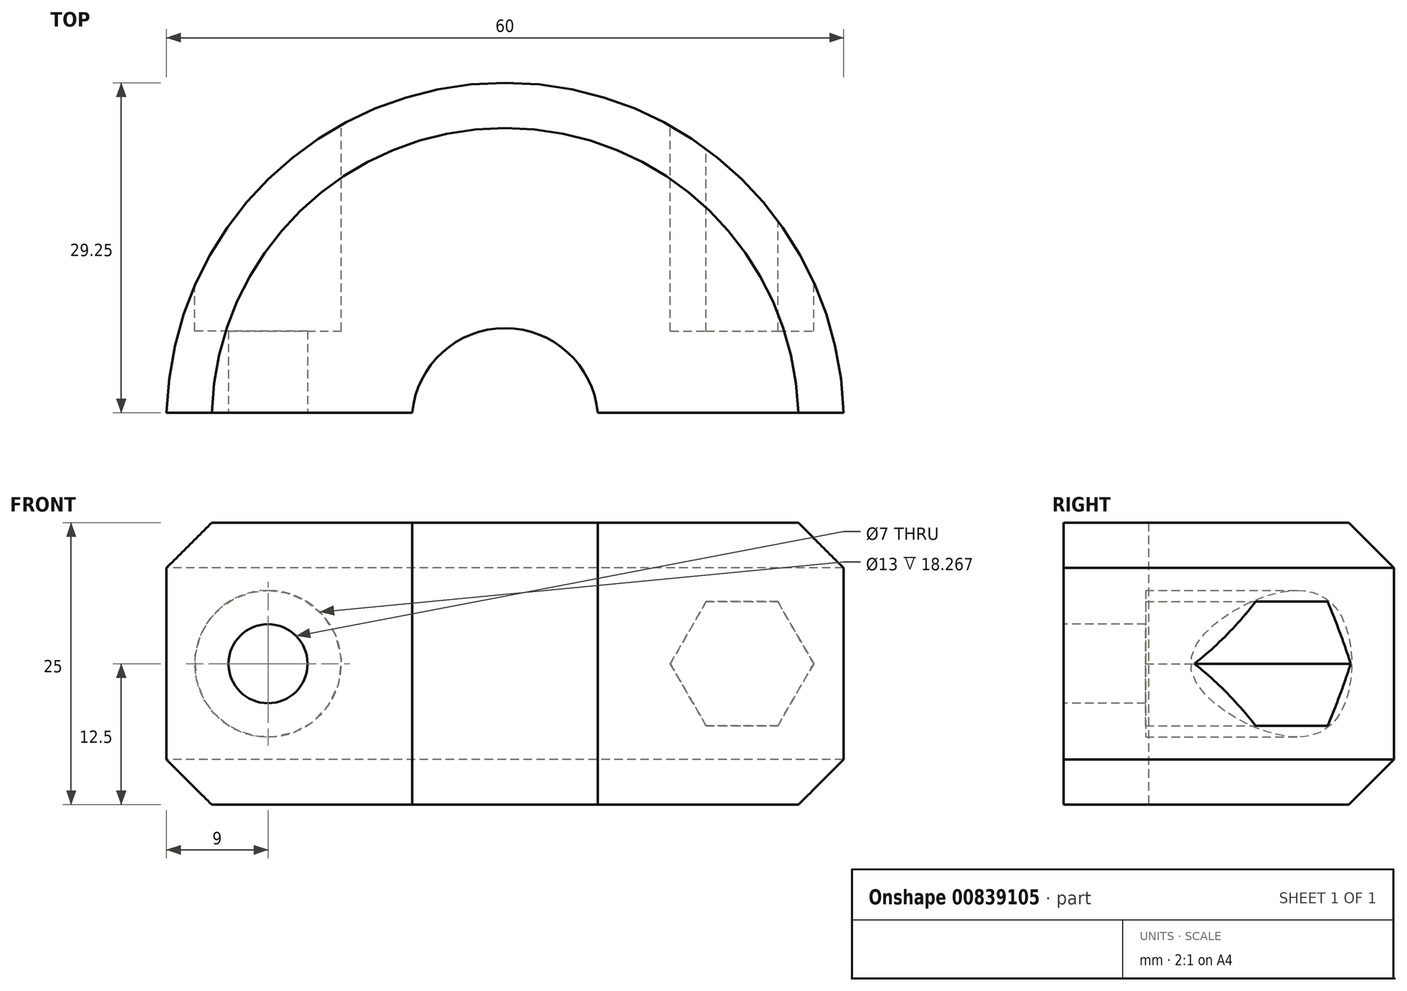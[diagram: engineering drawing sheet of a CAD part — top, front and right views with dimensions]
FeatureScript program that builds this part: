
annotation { "Feature Type Name" : "Feature", "Feature Type Description" : "" }
export const myFeature = defineFeature(function(context is Context, id is Id, definition is map)
    precondition{}
    {
        {
            var Q0;
            Q0=qCreatedBy(makeId("Top.planeOp"),FACE);
            var sketch = newSketch(context, id + "F0", { "sketchPlane" : qUnion([Q0])});
            skArc(sketch, "E0", {"start": v(30, 0) * mm, "mid": v(0, 30) * mm, "end": v(-30, 0) * mm});
            skArc(sketch, "E1", {"start": v(8.25, 0) * mm, "mid": v(0, 8.25) * mm, "end": v(-8.25, 0) * mm});
            skLineSegment(sketch, "E2", {"start": v(-41.2, 0) * mm, "end": v(58.71, 0) * mm, "construction": true});
            skLineSegment(sketch, "E3", {"start": v(-30, 0) * mm, "end": v(-8.25, 0) * mm});
            skLineSegment(sketch, "E4", {"start": v(8.25, 0) * mm, "end": v(30, 0) * mm});
            skSolve(sketch);
        }
        {
            var Q0;
            Q0=makeQuery(id+"F0.imprint","IMPRINT",FACE,{"disambiguationData":[TD([[makeQuery(id+"F0.imprint","IMPRINT",EDGE,{"derivedFrom":sQuery(id+"F0.wireOp",EDGE,"E0")}),1.0]])]});
            extrude(context, id + "F1", {"entities" : qUnion([Q0]), "depth" : 25 * mm, "offsetDistance" : 25 * mm});
        }
        {
            var Q0;
            Q0=makeQuery(id+"F1.opExtrude","SWEPT_FACE",FACE,{"disambiguationData":[OSD([sQuery(id+"F0.wireOp",EDGE,"E3")])]});
            var sketch = newSketch(context, id + "F2", { "sketchPlane" : qUnion([Q0])});
            skCircle(sketch, "E5", {"center": v(-21, 12.5) * mm, "radius": 3.5 * mm});
            skLineSegment(sketch, "E6", {"start": v(32.43, 12.5) * mm, "end": v(-38.56, 12.5) * mm, "construction": true});
            skPoint(sketch, "E6.startSnap0", {"position": v(-30, 12.5) * mm});
            skLineSegment(sketch, "E7", {"start": v(0, 0) * mm, "end": v(0, 34.25) * mm, "construction": true});
            skCircle(sketch, "E8.MirrorC", {"center": v(21, 12.5) * mm, "radius": 3.5 * mm});
            skSolve(sketch);
        }
        {
            var Q0;
            Q0=makeQuery(id+"F2.imprint","IMPRINT",FACE,{"disambiguationData":[TD([[makeQuery(id+"F2.imprint","IMPRINT",EDGE,{"derivedFrom":sQuery(id+"F2.wireOp",EDGE,"E5")}),1.0]])]});
            var Q1;
            Q1=makeQuery(id+"F2.imprint","IMPRINT",FACE,{"disambiguationData":[TD([[makeQuery(id+"F2.imprint","IMPRINT",EDGE,{"derivedFrom":sQuery(id+"F2.wireOp",EDGE,"E8.MirrorC")}),-1.0]])]});
            extrude(context, id + "F3", {"entities" : qUnion([Q0, Q1]), "operationType" : NewBodyOperationType.REMOVE, "oppositeDirection" : true, "depth" : 25 * mm, "offsetDistance" : 25 * mm});
        }
        {
            var Q0;
            Q0=qCreatedBy(makeId("Front.planeOp"),FACE);
            cPlane(context, id + "F4", {"entities" : qUnion([Q0]), "cplaneType" : CPlaneType.OFFSET, "offset" : 30 * mm, "oppositeDirection" : true, "width" : 150 * mm, "height" : 150 * mm});
        }
        {
            var Q0;
            Q0=qCreatedBy(id+"F4.planeOp",FACE);
            var sketch = newSketch(context, id + "F5", { "sketchPlane" : qUnion([Q0])});
            skCircle(sketch, "E9.cCircle", {"center": v(21, 12.5) * mm, "radius": 6.35 * mm, "construction": true});
            skLineSegment(sketch, "E9.0", {"start": v(24.18, 18) * mm, "end": v(27.35, 12.5) * mm});
            skLineSegment(sketch, "E9.1", {"start": v(27.35, 12.5) * mm, "end": v(24.18, 7) * mm});
            skLineSegment(sketch, "E9.2", {"start": v(24.18, 7) * mm, "end": v(17.82, 7) * mm});
            skLineSegment(sketch, "E9.3", {"start": v(17.82, 7) * mm, "end": v(14.65, 12.5) * mm});
            skLineSegment(sketch, "E9.4", {"start": v(14.65, 12.5) * mm, "end": v(17.82, 18) * mm});
            skLineSegment(sketch, "E9.5", {"start": v(17.82, 18) * mm, "end": v(24.18, 18) * mm});
            skCircle(sketch, "E10", {"center": v(-21, 12.5) * mm, "radius": 6.5 * mm});
            skSolve(sketch);
        }
        {
            var Q0;
            Q0=makeQuery(id+"F5.imprint","IMPRINT",FACE,{"disambiguationData":[TD([[makeQuery(id+"F5.imprint","IMPRINT",EDGE,{"derivedFrom":sQuery(id+"F5.wireOp",EDGE,"E9.0")}),-1.0]])]});
            var Q1;
            Q1=makeQuery(id+"F5.imprint","IMPRINT",FACE,{"disambiguationData":[TD([[makeQuery(id+"F5.imprint","IMPRINT",EDGE,{"derivedFrom":sQuery(id+"F5.wireOp",EDGE,"E10")}),1.0]])]});
            extrude(context, id + "F6", {"entities" : qUnion([Q0, Q1]), "operationType" : NewBodyOperationType.REMOVE, "depth" : 22 * mm, "offsetDistance" : 25 * mm});
        }
        {
            var Q0;
            Q0=makeQuery(id+"F1.opExtrude","CAP_FACE",FACE,{"disambiguationData":[OSD([sQuery(id+"F0.wireOp",EDGE,"E0"),sQuery(id+"F0.wireOp",EDGE,"E1"),sQuery(id+"F0.wireOp",EDGE,"E3"),sQuery(id+"F0.wireOp",EDGE,"E4")])],"isStart":false});
            var sketch = newSketch(context, id + "F7", { "sketchPlane" : qUnion([Q0])});
            skLineSegment(sketch, "E11.bottom", {"start": v(-30, 0) * mm, "end": v(30, 0) * mm});
            skLineSegment(sketch, "E11.top", {"start": v(-30, 0.75) * mm, "end": v(30, 0.75) * mm});
            skLineSegment(sketch, "E11.left", {"start": v(-30, 0) * mm, "end": v(-30, 0.75) * mm});
            skLineSegment(sketch, "E11.right", {"start": v(30, 0) * mm, "end": v(30, 0.75) * mm});
            skSolve(sketch);
        }
        {
            var Q0;
            Q0 = qSketchRegion(id + "F7", true);
            extrude(context, id + "F8", {"entities" : qUnion([Q0]), "operationType" : NewBodyOperationType.REMOVE, "oppositeDirection" : true, "depth" : 25 * mm, "offsetDistance" : 25 * mm});
        }
        {
            var Q0;
            Q0=makeQuery(id+"F1.opExtrude","CAP_EDGE",EDGE,{"disambiguationData":[OSD([sQuery(id+"F0.wireOp",EDGE,"E0")])],"isStart":false});
            var Q1;
            Q1=makeQuery(id+"F1.opExtrude","CAP_EDGE",EDGE,{"disambiguationData":[OSD([sQuery(id+"F0.wireOp",EDGE,"E0")])],"isStart":true});
            chamfer(context, id + "F9", {"entities" : qUnion([Q0, Q1]), "width" : 4 * mm, "tangentPropagation" : true});
        }
    });
